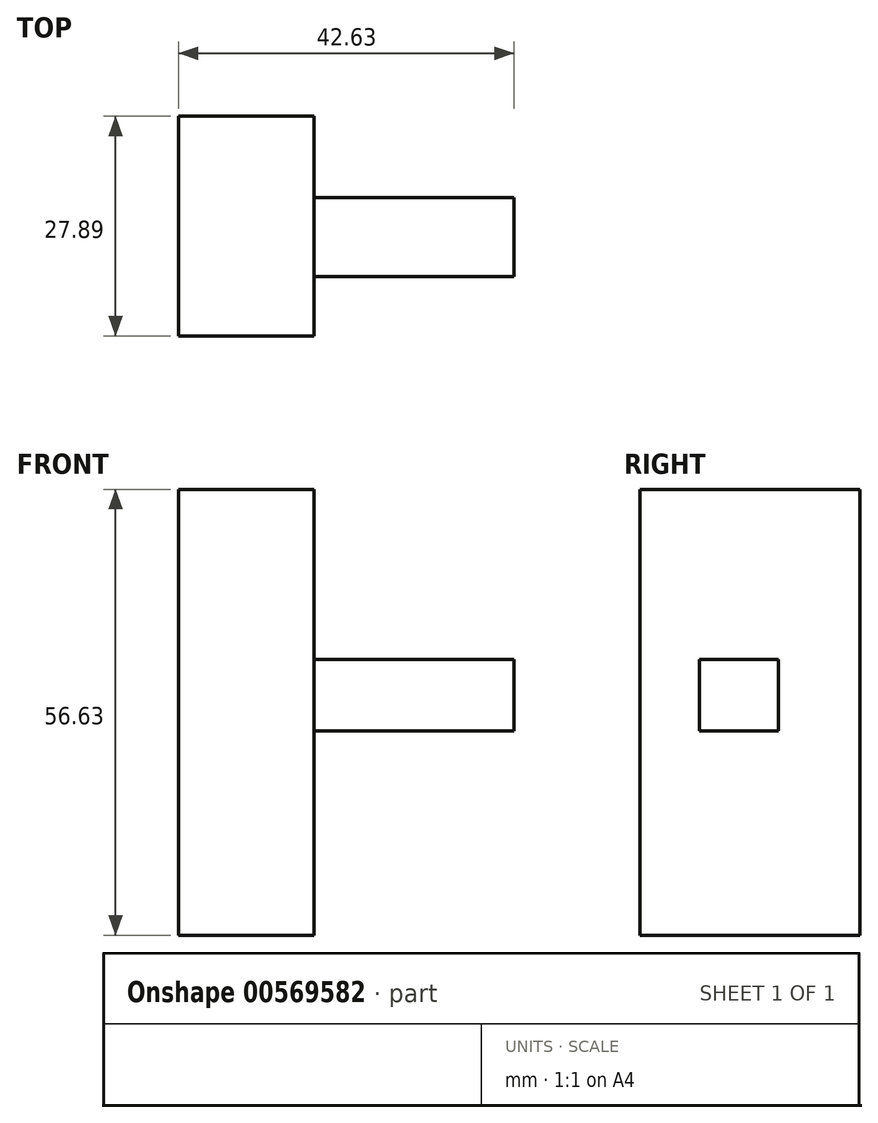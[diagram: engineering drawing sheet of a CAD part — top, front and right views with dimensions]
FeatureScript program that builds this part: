
annotation { "Feature Type Name" : "Feature", "Feature Type Description" : "" }
export const myFeature = defineFeature(function(context is Context, id is Id, definition is map)
    precondition{}
    {
        {
            var Q0;
            Q0=qCreatedBy(makeId("Front.planeOp"),FACE);
            var sketch = newSketch(context, id + "F0", { "sketchPlane" : qUnion([Q0])});
            skLineSegment(sketch, "E0.bottom", {"start": v(-17.23, 56.63) * mm, "end": v(0, 56.63) * mm});
            skLineSegment(sketch, "E0.top", {"start": v(-17.23, 0) * mm, "end": v(0, 0) * mm});
            skLineSegment(sketch, "E0.left", {"start": v(-17.23, 56.63) * mm, "end": v(-17.23, 0) * mm});
            skLineSegment(sketch, "E0.right", {"start": v(0, 56.63) * mm, "end": v(0, 0) * mm});
            skLineSegment(sketch, "E1.bottom", {"start": v(-17.23, 56.63) * mm, "end": v(-17.23, 56.63) * mm});
            skLineSegment(sketch, "E1.top", {"start": v(-17.23, 56.63) * mm, "end": v(-17.23, 56.63) * mm});
            skLineSegment(sketch, "E1.left", {"start": v(-17.23, 56.63) * mm, "end": v(-17.23, 56.63) * mm});
            skLineSegment(sketch, "E1.right", {"start": v(-17.23, 56.63) * mm, "end": v(-17.23, 56.63) * mm});
            skSolve(sketch);
        }
        {
            var Q0;
            Q0=makeQuery(id+"F0.imprint","IMPRINT",FACE,{"disambiguationData":[TD([[makeQuery(id+"F0.imprint","IMPRINT",EDGE,{"derivedFrom":sQuery(id+"F0.wireOp",EDGE,"E0.bottom")}),-1.0]])]});
            extrude(context, id + "F1", {"entities" : qUnion([Q0]), "depth" : 27.9 * mm, "offsetDistance" : 25.4 * mm});
        }
        {
            var Q0;
            Q0=makeQuery(id+"F1.opExtrude","SWEPT_FACE",FACE,{"disambiguationData":[OSD([sQuery(id+"F0.wireOp",EDGE,"E0.right")])]});
            var sketch = newSketch(context, id + "F2", { "sketchPlane" : qUnion([Q0])});
            skLineSegment(sketch, "E2.bottom", {"start": v(-20.32, 35.04) * mm, "end": v(-10.32, 35.04) * mm});
            skLineSegment(sketch, "E2.top", {"start": v(-20.32, 25.97) * mm, "end": v(-10.32, 25.97) * mm});
            skLineSegment(sketch, "E2.left", {"start": v(-20.32, 35.04) * mm, "end": v(-20.32, 25.97) * mm});
            skLineSegment(sketch, "E2.right", {"start": v(-10.32, 35.04) * mm, "end": v(-10.32, 25.97) * mm});
            skSolve(sketch);
        }
        {
            var Q0;
            Q0=makeQuery(id+"F2.imprint","IMPRINT",FACE,{"disambiguationData":[TD([[makeQuery(id+"F2.imprint","IMPRINT",EDGE,{"derivedFrom":sQuery(id+"F2.wireOp",EDGE,"E2.bottom")}),-1.0]])]});
            extrude(context, id + "F3", {"entities" : qUnion([Q0]), "operationType" : NewBodyOperationType.ADD, "depth" : 25.4 * mm, "offsetDistance" : 25.4 * mm});
        }
    });
